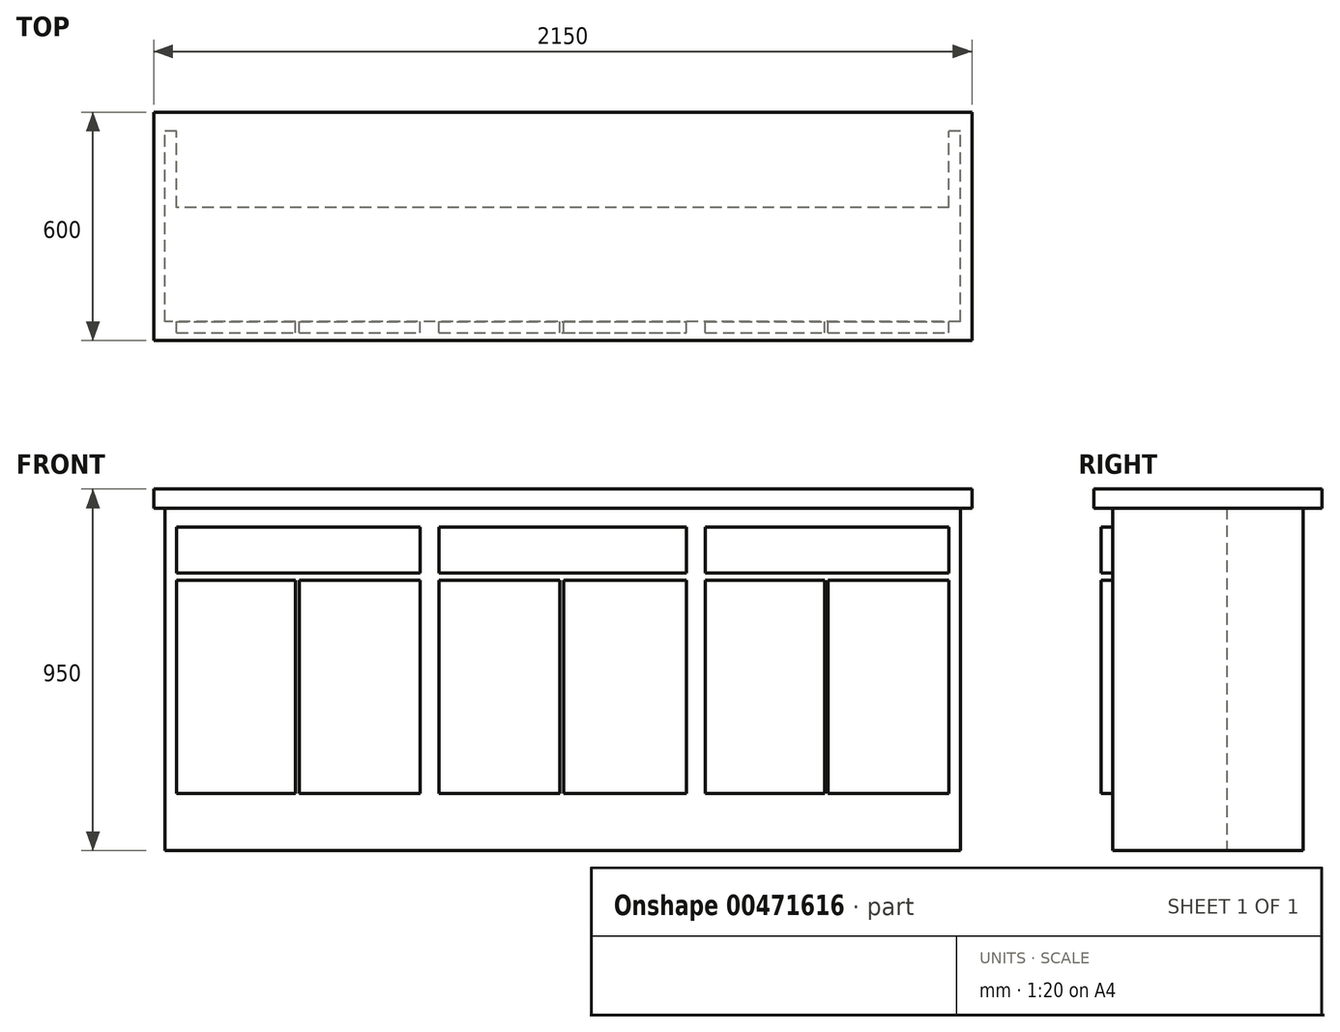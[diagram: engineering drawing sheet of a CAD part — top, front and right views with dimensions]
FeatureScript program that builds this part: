
annotation { "Feature Type Name" : "Feature", "Feature Type Description" : "" }
export const myFeature = defineFeature(function(context is Context, id is Id, definition is map)
    precondition{}
    {
        {
            var Q0;
            Q0=qCreatedBy(makeId("Top.planeOp"),FACE);
            var sketch = newSketch(context, id + "F0", { "sketchPlane" : qUnion([Q0])});
            skLineSegment(sketch, "E0.bottom", {"start": v(1075, -300) * mm, "end": v(-1075, -300) * mm});
            skLineSegment(sketch, "E0.top", {"start": v(1075, 300) * mm, "end": v(-1075, 300) * mm});
            skLineSegment(sketch, "E0.left", {"start": v(1075, -300) * mm, "end": v(1075, 300) * mm});
            skLineSegment(sketch, "E0.right", {"start": v(-1075, -300) * mm, "end": v(-1075, 300) * mm});
            skPoint(sketch, "E0.middle", {"position": v(0, 0) * mm});
            skSolve(sketch);
        }
        {
            var Q0;
            Q0=qSketchRegion(id+"F0",true);
            extrude(context, id + "F1", {"entities" : qUnion([Q0]), "depth" : 50 * mm});
        }
        {
            var Q0;
            Q0=qCreatedBy(makeId("Top.planeOp"),FACE);
            var sketch = newSketch(context, id + "F2", { "sketchPlane" : qUnion([Q0])});
            skLineSegment(sketch, "E1.bottom", {"start": v(1045, -250) * mm, "end": v(-1045, -250) * mm});
            skLineSegment(sketch, "E1.top", {"start": v(1045, 250) * mm, "end": v(-1045, 250) * mm});
            skLineSegment(sketch, "E1.left", {"start": v(1045, -250) * mm, "end": v(1045, 250) * mm});
            skLineSegment(sketch, "E1.right", {"start": v(-1045, -250) * mm, "end": v(-1045, 250) * mm});
            skPoint(sketch, "E1.middle", {"position": v(0, 0) * mm});
            skSolve(sketch);
        }
        {
            var Q0;
            Q0=qSketchRegion(id+"F2",true);
            extrude(context, id + "F3", {"entities" : qUnion([Q0]), "operationType" : NewBodyOperationType.ADD, "oppositeDirection" : true, "depth" : 900 * mm});
        }
        {
            var Q0;
            Q0=makeQuery(id+"F3.opExtrude","SWEPT_FACE",FACE,{"disambiguationData":[OSD([sQuery(id+"F2.wireOp",EDGE,"E1.bottom")])]});
            var sketch = newSketch(context, id + "F4", { "sketchPlane" : qUnion([Q0])});
            skLineSegment(sketch, "E2.bottom", {"start": v(-1015, -50) * mm, "end": v(-375, -50) * mm});
            skLineSegment(sketch, "E2.top", {"start": v(-1015, -170) * mm, "end": v(-375, -170) * mm});
            skLineSegment(sketch, "E2.left", {"start": v(-1015, -50) * mm, "end": v(-1015, -170) * mm});
            skLineSegment(sketch, "E2.right", {"start": v(-375, -50) * mm, "end": v(-375, -170) * mm});
            skLineSegment(sketch, "E3.bottom", {"start": v(-325, -50) * mm, "end": v(325, -50) * mm});
            skLineSegment(sketch, "E3.top", {"start": v(-325, -170) * mm, "end": v(325, -170) * mm});
            skLineSegment(sketch, "E3.left", {"start": v(-325, -50) * mm, "end": v(-325, -170) * mm});
            skLineSegment(sketch, "E3.right", {"start": v(325, -50) * mm, "end": v(325, -170) * mm});
            skLineSegment(sketch, "E4.bottom", {"start": v(375, -50) * mm, "end": v(1015, -50) * mm});
            skLineSegment(sketch, "E4.top", {"start": v(375, -170) * mm, "end": v(1015, -170) * mm});
            skLineSegment(sketch, "E4.left", {"start": v(375, -50) * mm, "end": v(375, -170) * mm});
            skLineSegment(sketch, "E4.right", {"start": v(1015, -50) * mm, "end": v(1015, -170) * mm});
            skLineSegment(sketch, "E5.bottom", {"start": v(-1015, -190) * mm, "end": v(-702.5, -190) * mm});
            skLineSegment(sketch, "E5.top", {"start": v(-1015, -750) * mm, "end": v(-702.5, -750) * mm});
            skLineSegment(sketch, "E5.left", {"start": v(-1015, -190) * mm, "end": v(-1015, -750) * mm});
            skLineSegment(sketch, "E5.right", {"start": v(-375, -190) * mm, "end": v(-375, -750) * mm});
            skLineSegment(sketch, "E6.bottom", {"start": v(-325, -190) * mm, "end": v(-7.5, -190) * mm});
            skLineSegment(sketch, "E6.top", {"start": v(-325, -750) * mm, "end": v(-7.5, -750) * mm});
            skLineSegment(sketch, "E6.left", {"start": v(-325, -190) * mm, "end": v(-325, -750) * mm});
            skLineSegment(sketch, "E6.right", {"start": v(325, -190) * mm, "end": v(325, -750) * mm});
            skLineSegment(sketch, "E7.bottom", {"start": v(375, -190) * mm, "end": v(687.5, -190) * mm});
            skLineSegment(sketch, "E7.top", {"start": v(375, -750) * mm, "end": v(687.5, -750) * mm});
            skLineSegment(sketch, "E7.left", {"start": v(375, -190) * mm, "end": v(375, -750) * mm});
            skLineSegment(sketch, "E7.right", {"start": v(1015, -190) * mm, "end": v(1015, -750) * mm});
            skLineSegment(sketch, "E8.left", {"start": v(-702.5, -190) * mm, "end": v(-702.5, -750) * mm});
            skLineSegment(sketch, "E8.right", {"start": v(-692.5, -190) * mm, "end": v(-692.5, -750) * mm});
            skLineSegment(sketch, "E9.left", {"start": v(-7.5, -190) * mm, "end": v(-7.5, -750) * mm});
            skLineSegment(sketch, "E9.right", {"start": v(2.5, -190) * mm, "end": v(2.5, -750) * mm});
            skLineSegment(sketch, "E10", {"start": v(0, -50) * mm, "end": v(0, 187.38) * mm, "construction": true});
            skLineSegment(sketch, "E11.left", {"start": v(687.5, -190) * mm, "end": v(687.5, -750) * mm});
            skLineSegment(sketch, "E11.right", {"start": v(697.5, -190) * mm, "end": v(697.5, -750) * mm});
            skLineSegment(sketch, "E12.trimOffspring", {"start": v(-692.5, -190) * mm, "end": v(-375, -190) * mm});
            skLineSegment(sketch, "E13.trimOffspring", {"start": v(-692.5, -750) * mm, "end": v(-375, -750) * mm});
            skLineSegment(sketch, "E14.trimOffspring", {"start": v(2.5, -750) * mm, "end": v(325, -750) * mm});
            skLineSegment(sketch, "E15.trimOffspring", {"start": v(2.5, -190) * mm, "end": v(325, -190) * mm});
            skLineSegment(sketch, "E16.trimOffspring", {"start": v(697.5, -750) * mm, "end": v(1015, -750) * mm});
            skLineSegment(sketch, "E17.trimOffspring", {"start": v(697.5, -190) * mm, "end": v(1015, -190) * mm});
            skSolve(sketch);
        }
        {
            var Q0;
            Q0=qSketchRegion(id+"F4",true);
            extrude(context, id + "F5", {"entities" : qUnion([Q0]), "operationType" : NewBodyOperationType.ADD, "depth" : 30 * mm});
        }
        {
            var Q0;
            Q0=makeQuery(id+"F3.opExtrude","SWEPT_FACE",FACE,{"disambiguationData":[OSD([sQuery(id+"F2.wireOp",EDGE,"E1.top")])]});
            var sketch = newSketch(context, id + "F6", { "sketchPlane" : qUnion([Q0])});
            skLineSegment(sketch, "E18.bottom", {"start": v(-1015, 0) * mm, "end": v(1015, 0) * mm});
            skLineSegment(sketch, "E18.top", {"start": v(-1015, -900) * mm, "end": v(1015, -900) * mm});
            skLineSegment(sketch, "E18.left", {"start": v(-1015, 0) * mm, "end": v(-1015, -900) * mm});
            skLineSegment(sketch, "E18.right", {"start": v(1015, 0) * mm, "end": v(1015, -900) * mm});
            skSolve(sketch);
        }
        {
            var Q0;
            Q0=qSketchRegion(id+"F6",true);
            extrude(context, id + "F7", {"entities" : qUnion([Q0]), "operationType" : NewBodyOperationType.REMOVE, "oppositeDirection" : true, "depth" : 200 * mm});
        }
    });
